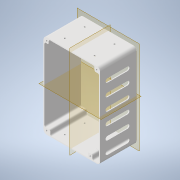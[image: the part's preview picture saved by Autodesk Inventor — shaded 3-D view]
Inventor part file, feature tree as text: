
AUTODESK INVENTOR PART (.ipt)
format: ipt  version: 2022 (Build 260153000, 153)  size: 240,640 bytes
history: native  units: mm
features: plane x4, sketch x3, extrude x2, other x2, fillet x1, pattern_linear x1, hole x1, reference x1, projected_geometry x1
ambient origin geometry x8: Origin, YZ Plane, XZ Plane, XY Plane, X Axis, Y Axis, Z Axis, Center Point
bodies: Volumenkörper1 (feature_tree)
feature tree (16):
  plane  "Arbeitsebene1"
  sketch  "Skizze1"  dims[d0=1.5mm d1=3.0mm d2=3.0mm]
  plane  "Arbeitsebene2"
  extrude  "Extrusion1"  Depth=3.0mm
  fillet  "Rundung1"  Radius=3.0mm
  extrude  "Extrusion4"  Depth=7.0mm
  pattern_linear  "Rechteckige Anordnung2"  Spacing1=7.0mm  [1 undecoded]
  plane  "Arbeitsebene3"
  plane  "Arbeitsebene4"
  hole  "Bohrung1"  [1 undecoded]
  reference  "Referenz1"
  sketch  "Skizze4"  dims[d3=55.0mm d4=0.0mm d5=7.0mm]
  sketch  "Skizze5"  dims[d6=7.0mm d7=7.0mm d8=7.0mm d9=10.0mm d10=2.8mm d13=2.0mm d29=6.0mm d30=55.0mm d31=0.0mm d32=60.0mm d34=18.9mm d35=45.0mm d36=30.0mm d37=2.8mm d38=6.0mm d39=4.0mm d40=2.0mm d41=90.0deg d42=8.0mm d43=20.594885mm]
  projected_geometry  "Projizierte Kontur2"
  other  "Omniscope_new_v0.iam"
  other  "Omniscope_Base_v0:1"
note: 2 required parameter values undecoded (feature->parameter linkage not recoverable at this tier; creation-order binding heuristic only, values carry confidence <= 0.55)
